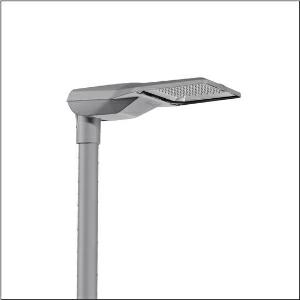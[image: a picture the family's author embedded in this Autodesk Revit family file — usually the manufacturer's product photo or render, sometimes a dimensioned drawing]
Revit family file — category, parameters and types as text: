
# Revit family: streetlight_sl_21_midi___st0_5a_5xe7b33a08lb_127a
name_source: partatom
category: Lighting Fixtures
units: mm (PartAtom-declared; Revit-internal decimal feet)

## family parameters
Cut with Voids When Loaded = No
Host = Face
Light Source = No
Part Type = Normal
Room Calculation Point = No
Round Connector Dimension = Use Diameter
Shared = No

## types (1)
- --- (1 x LED, 14340 lm, 98.3 W, 3000K)
    Apparent Load = 98 VA
    CIE Flux Codes = 41 75 97 100 100
    Color Rendering = 70
    Color Temperature = 3000K
    Default Elevation = 1800 mm
    Description = Streetlight SL 21 midi, mast luminaire, primary light control with lens, of PMMA, primary optical cover: cover, of toughened safety glass, transparent, light distribution: ST0.5a, light emission: direct distribution, primary light characteristic: asymmetric, installation type: post-top, side-entry, LED, 3G 1.5mm², High Power LED, rated luminous flux: 14.340lm, luminous efficacy: 146lm/W, light colour: 730, colour temperature: 3000K, control: overheat protection, constant luminous flux control, time-dependent luminous flux control, flexible luminous flux parameterisation, mains connection: 220..240V, AC, 50/60Hz, connection cable pre-assembled, cable length: 10,5m, wiring characteristics: H07RN-F, start of lifetime: 98W, end of service life: 101W, reduction: 44W, luminaire housing, of diecast aluminium, powder-coated, Siteco® metallic grey (DB 702S), corrosivity category C5 mid according to DIN EN ISO 12944, please order mast flange separately, inclination adjustable: 0°, 5°, 10°, 15°, sealing non-destructively replaceable, multi-level sealing system, length: 644mm, width: 335mm, height: 110mm, mast flange for spigot size: 42mm (side-entry): 5XC10008XM4, 60/48mm (side-entry/post-top): 5XC10108XM2, 76/60mm (side-entry/post-top): 5XC10108XM1, protection rating (complete): IP66, insulation class (complete): insulation class II (safety insulation), certification: CE, ENEC, ENEC+, VDE, impact resistance: IK09, permissible operating ambient temperature for outdoor applications: -40..+50°C, standard-compliant lighting for roads and squares, packaging unit: 1 piece

Light Distribution: ST0.5a
    Height = 111 mm
    Lamp = 1 x LED
    Lamp Light Flux = 14340 lm
    Lamp Power = 98.3 W
    Lamp count = 1
    Length = 644 mm
    Luminous efficacy = 146 lm/W
    Manufacturer = Siteco
    ModVariant = No
    Model = 5XE7B33A08LB
    Number of Poles = 1
    OnlyDefault = Yes
    Power Factor = 1
    Product Name = Streetlight SL 21 midi | ST0.5a
    Product group = mast luminaire | pylon top
    ProductGroupID = 6100
    Protection Class = Protection class II
    Protection Degree = IP 66
    RLX_Detail_Level = 1
    RLX_Emergency_Light_Flux = 0 lm
    RLX_Emergency_Type = 0
    RLX_Emergency_Type_DB = No
    RlxData = <blob elided: 101841 chars, md5=4ccb2f0e>
    Socket = socket
    Standby Power = 0 W
    System Light Flux = 14340 lm
    System Power = 98 W
    Type Comments = factory setting: luminous flux: 100 % | Output Level: 100 % | 1020 mA
    Type Image = l_1004298.jpg
    URL = http://relux.com
    VarID = @adj_144043
    Voltage = 0 V
    Weight = 0.00 kg
    Width = 336 mm

## geometry (parser evidence)
native form markers: Blend x4, Sweep x9
no freeform markers — native parametric forms only
